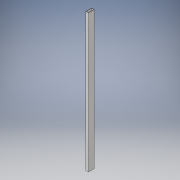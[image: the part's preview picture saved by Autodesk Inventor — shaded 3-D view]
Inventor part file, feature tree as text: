
AUTODESK INVENTOR PART (.ipt)
format: ipt  version: 2017 (Build 210142000, 142)  size: 99,840 bytes
history: native  units: in
note: dims shown in document units (in); Inventor stores cm internally (conversion verified against a paired STEP export)
features: extrude x1, sketch x1
ambient origin geometry x8: Origin, YZ Plane, XZ Plane, XY Plane, X Axis, Y Axis, Z Axis, Center Point
bodies: Solid1 (feature_tree)
feature tree (2):
  extrude  "Extrusion1"  Depth=2.0in
  sketch  "Sketch2"  dims[d2=1.0in d3=2.0in d4=0.75in d5=1.75in d6=0.125in d7=0.125in d8=48.0in d9=0.0in]
